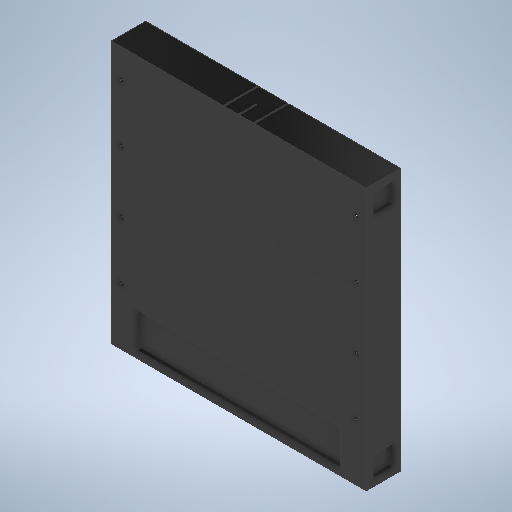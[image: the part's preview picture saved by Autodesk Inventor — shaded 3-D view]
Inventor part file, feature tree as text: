
AUTODESK INVENTOR PART (.ipt)
format: ipt  version: 2025.1 (Build 291241000, 241)  size: 1,494,528 bytes
history: native  units: mm
features: extrude x22, sketch x9, plane x1
ambient origin geometry x8: Origin, YZ Plane, XZ Plane, XY Plane, X Axis, Y Axis, Z Axis, Center Point
bodies: Volumenkörper1 (feature_tree)
feature tree (32):
  extrude  "Extrusion1"  Depth=178.0mm
  extrude  "Extrusion2"  Depth=2.0mm
  extrude  "Extrusion3"  Depth=2.0mm
  extrude  "Extrusion4"  Depth=24.0mm TaperAngle=0.0deg
  extrude  "Extrusion5"  TaperAngle=45.0deg  [1 undecoded]
  extrude  "Extrusion8"  TaperAngle=45.0deg  [1 undecoded]
  plane  "Arbeitsebene1"
  extrude  "Extrusion9"  Depth=181.0mm TaperAngle=0.0deg
  extrude  "Extrusion10"  Depth=2.0mm TaperAngle=0.0deg
  extrude  "Extrusion11"  Depth=24.0mm
  extrude  "Extrusion12"  Depth=14.0mm
  extrude  "Extrusion13"  Depth=14.0mm
  extrude  "Extrusion14"  Depth=3.0mm TaperAngle=0.0deg
  extrude  "Extrusion15"  Depth=5.0mm
  extrude  "Extrusion16"  Depth=24.5mm
  extrude  "Extrusion17"  Depth=10.0mm
  extrude  "Extrusion20"  Depth=10.0mm
  extrude  "Extrusion21"  Depth=3.0mm TaperAngle=0.0deg
  extrude  "Extrusion22"  Depth=3.0mm TaperAngle=0.0deg
  extrude  "Extrusion23"  Depth=2.0mm
  extrude  "Extrusion25"  Depth=24.5mm
  extrude  "Extrusion26"  Depth=3.0mm
  extrude  "Extrusion27"  Depth=3.0mm
  sketch  "Skizze3"  dims[d0=183.0mm d1=178.0mm]
  sketch  "Skizze9"  dims[d2=24.0mm d3=0.0mm d4=2.0mm]
  sketch  "Skizze10"  dims[d5=2.0mm d6=17.0mm]
  sketch  "Skizze11"  dims[d7=24.0mm d8=156.5mm d9=0.0mm]
  sketch  "Skizze12"  dims[d10=5.0mm d11=45.0deg]
  sketch  "Skizze14"  dims[d12=45.0deg d13=45.0deg]
  sketch  "Skizze30"  dims[d14=45.0deg d15=181.0mm d16=0.0mm]
  sketch  "Skizze36"  dims[d17=5.0mm d18=0.0mm d19=2.0mm d20=0.0mm]
  sketch  "Skizze42"  dims[d38=24.0mm d39=24.0mm d40=14.0mm d41=14.0mm d42=3.0mm d43=0.0mm d44=5.0mm d45=24.5mm d46=6.0mm d47=6.0mm d48=3.0mm d49=0.0mm d50=3.0mm d51=0.0mm d52=2.0mm d53=24.5mm d54=3.0mm d55=3.0mm d56=181.0mm d57=0.0mm d58=20.0mm d59=10.0mm d60=10.0mm d61=10.0mm d62=10.0mm d63=10.0mm d64=10.0mm d65=10.0mm d66=10.0mm d67=10.0mm d68=10.0mm d69=10.0mm d70=10.0mm d71=10.0mm d72=8.0mm d73=2.0mm d74=2.0mm d75=8.0mm d76=2.0mm d77=2.0mm d78=114.0mm d79=0.0mm d80=178.0mm d81=14.5mm d82=1.0mm d83=1.0mm d84=154.0mm d85=154.0mm d86=1.0mm d87=0.0mm d88=1.0mm d89=0.0mm d90=130.0mm d91=130.0mm d94=1.0mm d98=3.0mm d99=0.0mm d100=3.0mm d101=0.0mm d102=3.0mm d103=0.0mm d140=24.0mm d141=24.0mm d142=24.0mm d143=24.0mm d144=24.0mm d145=24.0mm d146=24.0mm d147=5.0mm d148=0.0mm d161=5.0mm d162=5.0mm d163=5.0mm d164=5.0mm d165=5.0mm d166=5.0mm d167=5.0mm d168=5.0mm d169=14.0mm d170=14.0mm d171=14.0mm d172=14.0mm d173=14.0mm d174=14.0mm d175=14.0mm d176=14.0mm d177=3.0mm d178=0.0mm d179=20.0mm d180=2.0mm d181=2.0mm d182=1.0mm d183=0.0mm d184=20.0mm d185=0.0mm d186=130.0mm d187=14.0mm d198=168.5mm d199=0.0mm d200=5.0mm d201=0.0mm d202=5.7mm d203=12.0mm d204=12.0mm d205=20.0mm d206=40.0mm d207=40.0mm d208=40.0mm d209=5.7mm d210=5.7mm d211=5.7mm d212=3.4mm d213=3.4mm d214=3.4mm d215=3.4mm d216=3.4mm d217=3.4mm d218=3.4mm d219=3.4mm d220=0.0mm d221=0.0mm d222=0.0mm d223=0.0mm d224=6.0mm d225=6.0mm d226=6.0mm d227=6.0mm d228=6.0mm d229=6.0mm d230=6.0mm d231=6.0mm d232=10.0mm d233=0.0mm]
note: 2 required parameter values undecoded (feature->parameter linkage not recoverable at this tier; creation-order binding heuristic only, values carry confidence <= 0.55)
